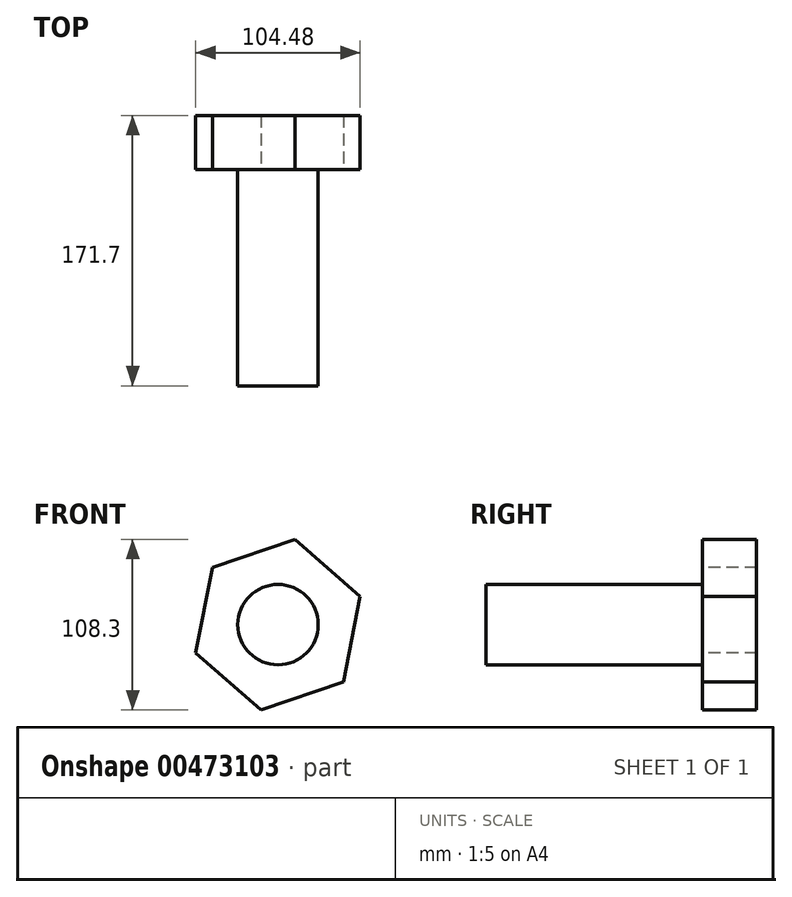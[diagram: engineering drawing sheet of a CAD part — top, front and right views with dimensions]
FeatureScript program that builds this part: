
annotation { "Feature Type Name" : "Feature", "Feature Type Description" : "" }
export const myFeature = defineFeature(function(context is Context, id is Id, definition is map)
    precondition{}
    {
        {
            var Q0;
            Q0=qCreatedBy(makeId("Front.planeOp"),FACE);
            var sketch = newSketch(context, id + "F0", { "sketchPlane" : qUnion([Q0])});
            skCircle(sketch, "E0.cCircle", {"center": v(0, 0) * mm, "radius": 47.8 * mm, "construction": true});
            skLineSegment(sketch, "E0.0", {"start": v(10.7, 54.15) * mm, "end": v(52.24, 17.81) * mm});
            skLineSegment(sketch, "E0.1", {"start": v(52.24, 17.81) * mm, "end": v(41.55, -36.33) * mm});
            skLineSegment(sketch, "E0.2", {"start": v(41.55, -36.33) * mm, "end": v(-10.7, -54.15) * mm});
            skLineSegment(sketch, "E0.3", {"start": v(-10.7, -54.15) * mm, "end": v(-52.24, -17.81) * mm});
            skLineSegment(sketch, "E0.4", {"start": v(-52.24, -17.81) * mm, "end": v(-41.55, 36.33) * mm});
            skLineSegment(sketch, "E0.5", {"start": v(-41.55, 36.33) * mm, "end": v(10.7, 54.15) * mm});
            skPoint(sketch, "E0.0.midPoint", {"position": v(31.46, 35.98) * mm});
            skSolve(sketch);
        }
        {
            var Q0;
            Q0 = qSketchRegion(id + "F0", true);
            extrude(context, id + "F1", {"entities" : qUnion([Q0]), "oppositeDirection" : true, "depth" : 34.3 * mm});
        }
        {
            var Q0;
            Q0=makeQuery(id+"F1.opExtrude","CAP_FACE",FACE,{"disambiguationData":[OSD([sQuery(id+"F0.wireOp",EDGE,"E0.0"),sQuery(id+"F0.wireOp",EDGE,"E0.1"),sQuery(id+"F0.wireOp",EDGE,"E0.2"),sQuery(id+"F0.wireOp",EDGE,"E0.3"),sQuery(id+"F0.wireOp",EDGE,"E0.4"),sQuery(id+"F0.wireOp",EDGE,"E0.5")])],"isStart":true});
            var sketch = newSketch(context, id + "F2", { "sketchPlane" : qUnion([Q0])});
            skCircle(sketch, "E1", {"center": v(0, 0) * mm, "radius": 25.53 * mm});
            skSolve(sketch);
        }
        {
            var Q0;
            Q0=makeQuery(id+"F2.imprint","IMPRINT",FACE,{"disambiguationData":[TD([[makeQuery(id+"F2.imprint","IMPRINT",EDGE,{"derivedFrom":sQuery(id+"F2.wireOp",EDGE,"E1")}),1.0]])]});
            extrude(context, id + "F3", {"entities" : qUnion([Q0]), "operationType" : NewBodyOperationType.ADD, "depth" : 137.4 * mm});
        }
        {
            var Q0;
            Q0=makeQuery(id+"F3.opExtrude","CAP_FACE",FACE,{"disambiguationData":[OSD([sQuery(id+"F2.wireOp",EDGE,"E1")])],"isStart":false});
            var sketch = newSketch(context, id + "F4", { "sketchPlane" : qUnion([Q0])});
            skCircle(sketch, "E2", {"center": v(0, 0) * mm, "radius": 11.71 * mm});
            skSolve(sketch);
        }
        {
            var Q0;
            Q0=makeQuery(id+"F4.imprint","IMPRINT",FACE,{"disambiguationData":[TD([[makeQuery(id+"F4.imprint","IMPRINT",EDGE,{"derivedFrom":sQuery(id+"F4.wireOp",EDGE,"E2")}),1.0]])]});
            extrude(context, id + "F5", {"entities" : qUnion([Q0]), "operationType" : NewBodyOperationType.ADD, "oppositeDirection" : true, "depth" : 168.4 * mm});
        }
    });
